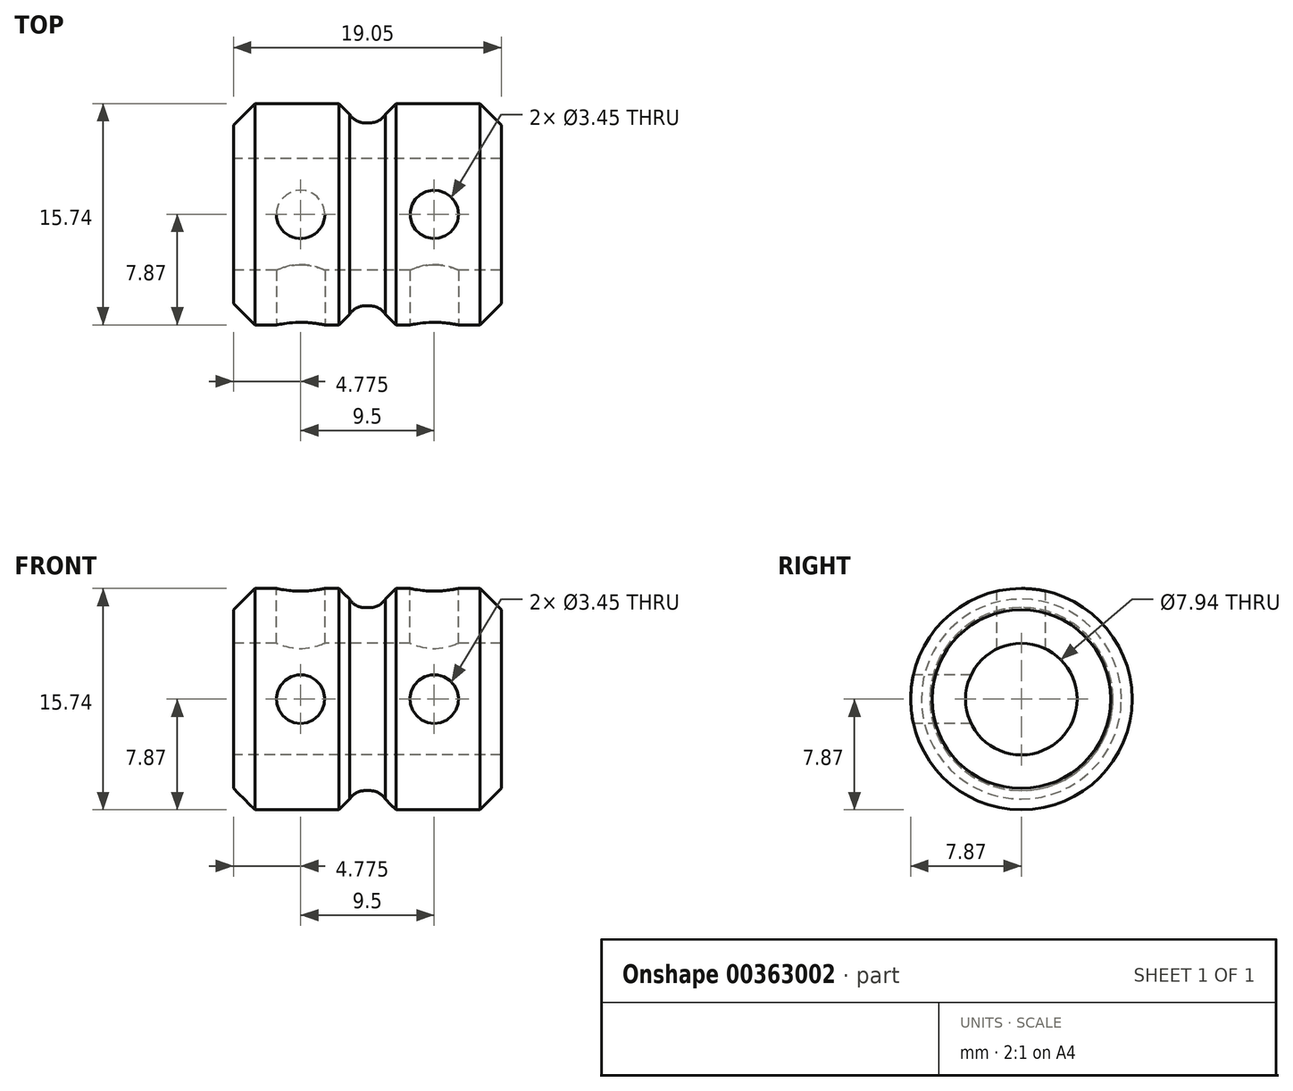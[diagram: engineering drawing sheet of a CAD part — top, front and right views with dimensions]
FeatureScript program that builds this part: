
annotation { "Feature Type Name" : "Feature", "Feature Type Description" : "" }
export const myFeature = defineFeature(function(context is Context, id is Id, definition is map)
    precondition{}
    {
        {
            var Q0;
            Q0=qCreatedBy(makeId("Right.planeOp"),FACE);
            var sketch = newSketch(context, id + "F0", { "sketchPlane" : qUnion([Q0])});
            skCircle(sketch, "E0", {"center": v(0, 0) * mm, "radius": 3.97 * mm});
            skCircle(sketch, "E1", {"center": v(0, 0) * mm, "radius": 7.87 * mm});
            skSolve(sketch);
        }
        {
            var Q0;
            Q0=makeQuery(id+"F0.imprint","IMPRINT",FACE,{"disambiguationData":[TD([[makeQuery(id+"F0.imprint","IMPRINT",EDGE,{"derivedFrom":sQuery(id+"F0.wireOp",EDGE,"E0")}),-1.0]])]});
            extrude(context, id + "F1", {"entities" : qUnion([Q0]), "depth" : 19.05 * mm});
        }
        {
            var Q0;
            Q0=makeQuery(id+"F1.opExtrude","CAP_EDGE",EDGE,{"disambiguationData":[OSD([sQuery(id+"F0.wireOp",EDGE,"E1")])],"isStart":false});
            var Q1;
            Q1=makeQuery(id+"F1.opExtrude","CAP_EDGE",EDGE,{"disambiguationData":[OSD([sQuery(id+"F0.wireOp",EDGE,"E1")])],"isStart":true});
            chamfer(context, id + "F2", {"entities" : qUnion([Q0, Q1]), "chamferType" : ChamferType.OFFSET_ANGLE, "width" : 1.52 * mm, "oppositeDirection" : false, "angle" : 45 * degree, "tangentPropagation" : true});
        }
        {
            var Q0;
            Q0=qCreatedBy(makeId("Top.planeOp"),FACE);
            cPlane(context, id + "F3", {"entities" : qUnion([Q0]), "cplaneType" : CPlaneType.OFFSET, "offset" : 8.64 * mm, "width" : 152.4 * mm, "height" : 152.4 * mm});
        }
        {
            var Q0;
            Q0=qCreatedBy(id+"F3.planeOp",FACE);
            var sketch = newSketch(context, id + "F4", { "sketchPlane" : qUnion([Q0])});
            skPoint(sketch, "E2", {"position": v(4.78, 0) * mm});
            skPoint(sketch, "E3", {"position": v(14.27, 0) * mm});
            skSolve(sketch);
        }
        {
            var Q0;
            Q0=sQuery(id+"F4.wireOp",VERTEX,"E2");
            var Q1;
            Q1=sQuery(id+"F4.wireOp",VERTEX,"E3");
            var Q2;
            Q2=makeQuery(id+"F1.opExtrude","SWEPT_BODY",BODY,{"disambiguationData":[OSD([sQuery(id+"F0.wireOp",EDGE,"E0"),sQuery(id+"F0.wireOp",EDGE,"E1")])]});
            hole(context, id + "F5", {"style" : HoleStyle.SIMPLE, "endStyle" : HoleEndStyle.BLIND, "standardTappedOrClearance" : lookupTablePath({ "standard" : "ANSI", "engagement" : "75%", "pitch" : "32 tpi", "size" : "#8", "type" : "Tapped" }), "standardBlindInLast" : lookupTablePath({ "standard" : "ANSI", "engagement" : "75%", "pitch" : "32 tpi", "size" : "#8", "type" : "Tapped" }), "holeDiameter" : 3.45 * mm, "showTappedDepth" : true, "holeDepth" : 9.5 * mm, "tappedDepth" : 7.11 * mm, "tapClearance" : 3, "locations" : qUnion([Q0, Q1]), "scope" : qUnion([Q2]), "majorDiameter" : 4.17 * mm});
        }
        {
            var Q0;
            Q0=qCreatedBy(makeId("Front.planeOp"),FACE);
            cPlane(context, id + "F6", {"entities" : qUnion([Q0]), "cplaneType" : CPlaneType.OFFSET, "offset" : 8.64 * mm, "width" : 152.4 * mm, "height" : 152.4 * mm});
        }
        {
            var Q0;
            Q0=qCreatedBy(id+"F6.planeOp",FACE);
            var sketch = newSketch(context, id + "F7", { "sketchPlane" : qUnion([Q0])});
            skPoint(sketch, "E4", {"position": v(4.78, 0) * mm});
            skPoint(sketch, "E5", {"position": v(14.27, 0) * mm});
            skSolve(sketch);
        }
        {
            var Q0;
            Q0=sQuery(id+"F7.wireOp",VERTEX,"E4");
            var Q1;
            Q1=sQuery(id+"F7.wireOp",VERTEX,"E5");
            var Q2;
            Q2=makeQuery(id+"F1.opExtrude","SWEPT_BODY",BODY,{"disambiguationData":[OSD([sQuery(id+"F0.wireOp",EDGE,"E0"),sQuery(id+"F0.wireOp",EDGE,"E1")])]});
            hole(context, id + "F8", {"style" : HoleStyle.SIMPLE, "endStyle" : HoleEndStyle.BLIND, "standardTappedOrClearance" : lookupTablePath({ "standard" : "ANSI", "engagement" : "75%", "pitch" : "32 tpi", "size" : "#8", "type" : "Tapped" }), "standardBlindInLast" : lookupTablePath({ "standard" : "ANSI", "engagement" : "75%", "pitch" : "32 tpi", "size" : "#8", "type" : "Tapped" }), "holeDiameter" : 3.45 * mm, "showTappedDepth" : true, "holeDepth" : 9.5 * mm, "tappedDepth" : 7.12 * mm, "tapClearance" : 3, "locations" : qUnion([Q0, Q1]), "scope" : qUnion([Q2]), "majorDiameter" : 4.17 * mm});
        }
        {
            var Q0;
            Q0=qCreatedBy(makeId("Front.planeOp"),FACE);
            var sketch = newSketch(context, id + "F9", { "sketchPlane" : qUnion([Q0])});
            skLineSegment(sketch, "E6.0", {"start": v(1.52, 7.87) * mm, "end": v(1.52, -7.87) * mm});
            skLineSegment(sketch, "E7.0", {"start": v(17.53, -7.87) * mm, "end": v(17.53, 7.87) * mm});
            skLineSegment(sketch, "E8", {"start": v(9.52, 8.94) * mm, "end": v(10.8, 8.94) * mm});
            skLineSegment(sketch, "E9", {"start": v(10.8, 8.94) * mm, "end": v(10.8, 6.51) * mm});
            skLineSegment(sketch, "E10", {"start": v(10.8, 6.51) * mm, "end": v(8.25, 6.51) * mm});
            skLineSegment(sketch, "E11", {"start": v(8.25, 6.51) * mm, "end": v(8.25, 8.94) * mm});
            skLineSegment(sketch, "E12", {"start": v(8.25, 8.94) * mm, "end": v(9.52, 8.94) * mm});
            skLineSegment(sketch, "E13", {"start": v(-1.55, 0) * mm, "end": v(-3.62, 0) * mm});
            skSolve(sketch);
        }
        {
            var Q0;
            Q0=makeQuery(id+"F9.imprint","IMPRINT",FACE,{"disambiguationData":[TD([[makeQuery(id+"F9.imprint","IMPRINT",EDGE,{"derivedFrom":sQuery(id+"F9.wireOp",EDGE,"E8")}),-1.0]])]});
            var Q1;
            Q1=sQuery(id+"F9.wireOp",EDGE,"E13");
            revolve(context, id + "F10", {"operationType" : NewBodyOperationType.REMOVE, "entities" : qUnion([Q0]), "axis" : qUnion([Q1]), "revolveType" : RevolveType.FULL, "oppositeDirection" : true});
        }
        {
            var Q0;
            Q0=makeQuery(id+"F10.boolean.opBoolean","INTERSECT",EDGE,{"derivedFrom":[makeQuery(id+"F1.opExtrude","SWEPT_FACE",FACE,{"disambiguationData":[OSD([sQuery(id+"F0.wireOp",EDGE,"E1")])]}),makeQuery(id+"F10.opRevolve","SWEPT_FACE",FACE,{"disambiguationData":[OSD([sQuery(id+"F9.wireOp",EDGE,"E11")])]})]});
            var Q1;
            Q1=makeQuery(id+"F10.boolean.opBoolean","INTERSECT",EDGE,{"derivedFrom":[makeQuery(id+"F1.opExtrude","SWEPT_FACE",FACE,{"disambiguationData":[OSD([sQuery(id+"F0.wireOp",EDGE,"E1")])]}),makeQuery(id+"F10.opRevolve","SWEPT_FACE",FACE,{"disambiguationData":[OSD([sQuery(id+"F9.wireOp",EDGE,"E9")])]})]});
            chamfer(context, id + "F11", {"entities" : qUnion([Q0, Q1]), "chamferType" : ChamferType.OFFSET_ANGLE, "width" : 0.76 * mm, "oppositeDirection" : false, "angle" : 45 * degree, "tangentPropagation" : true});
        }
        {
            var Q0;
            Q0=makeQuery(id+"F10.boolean.opBoolean","COPY",EDGE,{"derivedFrom":makeQuery(id+"F10.opRevolve","SWEPT_EDGE",EDGE,{"disambiguationData":[OSD([sQuery(id+"F9.wireOp",EDGE,"E10"),sQuery(id+"F9.wireOp",EDGE,"E11")])]})});
            var Q1;
            Q1=makeQuery(id+"F10.boolean.opBoolean","COPY",EDGE,{"derivedFrom":makeQuery(id+"F10.opRevolve","SWEPT_EDGE",EDGE,{"disambiguationData":[OSD([sQuery(id+"F9.wireOp",EDGE,"E9"),sQuery(id+"F9.wireOp",EDGE,"E10")])]})});
            fillet(context, id + "F12", {"entities" : qUnion([Q0, Q1]), "radius" : 1.27 * mm, "tangentPropagation" : true, "allowEdgeOverflow" : false});
        }
    });
